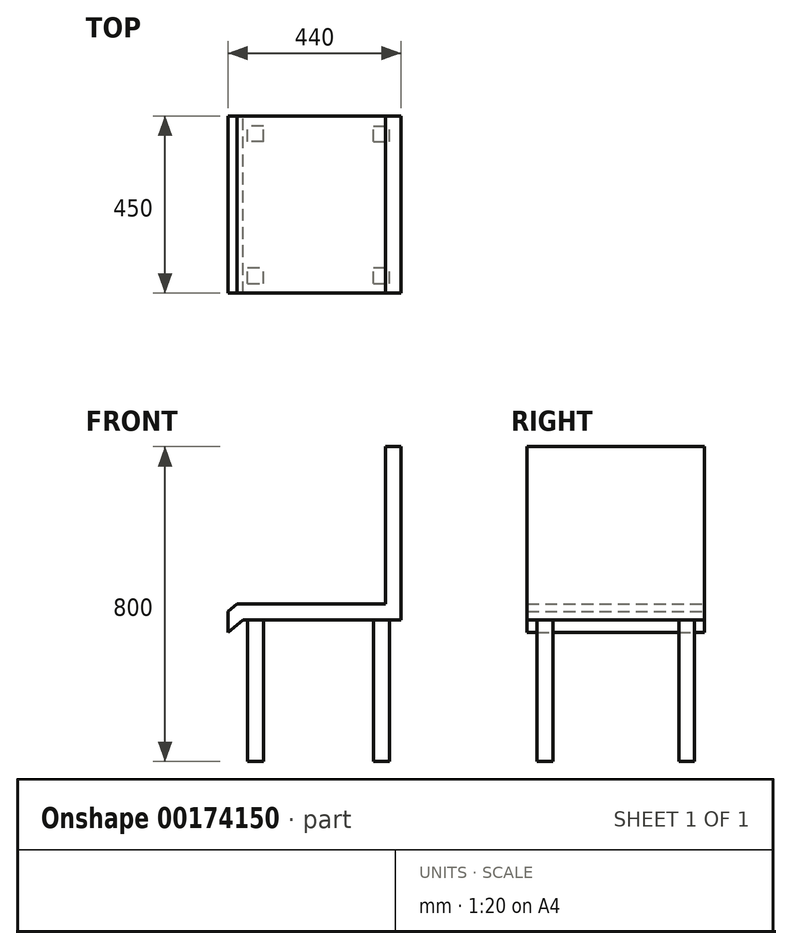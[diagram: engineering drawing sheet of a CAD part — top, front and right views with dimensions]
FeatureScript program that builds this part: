
annotation { "Feature Type Name" : "Feature", "Feature Type Description" : "" }
export const myFeature = defineFeature(function(context is Context, id is Id, definition is map)
    precondition{}
    {
        {
            var Q0;
            Q0=qCreatedBy(makeId("Front.planeOp"),FACE);
            var sketch = newSketch(context, id + "F0", { "sketchPlane" : qUnion([Q0])});
            skLineSegment(sketch, "E0", {"start": v(-250, 328.5) * mm, "end": v(-212.46, 360) * mm});
            skLineSegment(sketch, "E1", {"start": v(-212.46, 360) * mm, "end": v(190, 360) * mm});
            skLineSegment(sketch, "E2", {"start": v(190, 360) * mm, "end": v(190, 800) * mm});
            skLineSegment(sketch, "E3", {"start": v(190, 800) * mm, "end": v(150, 800) * mm});
            skLineSegment(sketch, "E4", {"start": v(150, 800) * mm, "end": v(150, 400) * mm});
            skLineSegment(sketch, "E5", {"start": v(150, 400) * mm, "end": v(-227.02, 400) * mm});
            skLineSegment(sketch, "E6", {"start": v(-227.02, 400) * mm, "end": v(-250, 380.72) * mm});
            skLineSegment(sketch, "E7", {"start": v(-250, 380.72) * mm, "end": v(-250, 328.5) * mm});
            skSolve(sketch);
        }
        {
            var Q0;
            Q0=makeQuery(id+"F0.imprint","IMPRINT",FACE,{"disambiguationData":[TD([[makeQuery(id+"F0.imprint","IMPRINT",EDGE,{"derivedFrom":sQuery(id+"F0.wireOp",EDGE,"E0")}),1.0]])]});
            extrude(context, id + "F1", {"entities" : qUnion([Q0]), "endBound" : BoundingType.SYMMETRIC, "depth" : 450 * mm});
        }
        {
            var Q0;
            Q0=qCreatedBy(makeId("Top.planeOp"),FACE);
            var sketch = newSketch(context, id + "F2", { "sketchPlane" : qUnion([Q0])});
            skLineSegment(sketch, "E8.bottom", {"start": v(-200, -200) * mm, "end": v(-160, -200) * mm});
            skLineSegment(sketch, "E8.top", {"start": v(-200, -160) * mm, "end": v(-160, -160) * mm});
            skLineSegment(sketch, "E8.left", {"start": v(-200, -200) * mm, "end": v(-200, -160) * mm});
            skLineSegment(sketch, "E8.right", {"start": v(-160, -200) * mm, "end": v(-160, -160) * mm});
            skLineSegment(sketch, "E9.bottom", {"start": v(120, -200) * mm, "end": v(160, -200) * mm});
            skLineSegment(sketch, "E9.top", {"start": v(120, -160) * mm, "end": v(160, -160) * mm});
            skLineSegment(sketch, "E9.left", {"start": v(120, -200) * mm, "end": v(120, -160) * mm});
            skLineSegment(sketch, "E9.right", {"start": v(160, -200) * mm, "end": v(160, -160) * mm});
            skLineSegment(sketch, "E10.bottom", {"start": v(-160, 160) * mm, "end": v(-200, 160) * mm});
            skLineSegment(sketch, "E10.top", {"start": v(-160, 200) * mm, "end": v(-200, 200) * mm});
            skLineSegment(sketch, "E10.left", {"start": v(-160, 160) * mm, "end": v(-160, 200) * mm});
            skLineSegment(sketch, "E10.right", {"start": v(-200, 160) * mm, "end": v(-200, 200) * mm});
            skLineSegment(sketch, "E11.bottom", {"start": v(120, 160) * mm, "end": v(160, 160) * mm});
            skLineSegment(sketch, "E11.top", {"start": v(120, 200) * mm, "end": v(160, 200) * mm});
            skLineSegment(sketch, "E11.left", {"start": v(120, 160) * mm, "end": v(120, 200) * mm});
            skLineSegment(sketch, "E11.right", {"start": v(160, 160) * mm, "end": v(160, 200) * mm});
            skSolve(sketch);
        }
        {
            var Q0;
            Q0=makeQuery(id+"F2.imprint","IMPRINT",FACE,{"disambiguationData":[TD([[makeQuery(id+"F2.imprint","IMPRINT",EDGE,{"derivedFrom":sQuery(id+"F2.wireOp",EDGE,"E9.bottom")}),1.0]])]});
            var Q1;
            Q1=makeQuery(id+"F2.imprint","IMPRINT",FACE,{"disambiguationData":[TD([[makeQuery(id+"F2.imprint","IMPRINT",EDGE,{"derivedFrom":sQuery(id+"F2.wireOp",EDGE,"E8.bottom")}),1.0]])]});
            var Q2;
            Q2=makeQuery(id+"F2.imprint","IMPRINT",FACE,{"disambiguationData":[TD([[makeQuery(id+"F2.imprint","IMPRINT",EDGE,{"derivedFrom":sQuery(id+"F2.wireOp",EDGE,"E10.bottom")}),-1.0]])]});
            var Q3;
            Q3=makeQuery(id+"F2.imprint","IMPRINT",FACE,{"disambiguationData":[TD([[makeQuery(id+"F2.imprint","IMPRINT",EDGE,{"derivedFrom":sQuery(id+"F2.wireOp",EDGE,"E11.bottom")}),1.0]])]});
            var Q4;
            Q4=makeQuery(id+"F1.opExtrude","SWEPT_BODY",BODY,{"disambiguationData":[OSD([sQuery(id+"F0.wireOp",EDGE,"E0"),sQuery(id+"F0.wireOp",EDGE,"E1"),sQuery(id+"F0.wireOp",EDGE,"E2"),sQuery(id+"F0.wireOp",EDGE,"E3"),sQuery(id+"F0.wireOp",EDGE,"E4"),sQuery(id+"F0.wireOp",EDGE,"E5"),sQuery(id+"F0.wireOp",EDGE,"E6"),sQuery(id+"F0.wireOp",EDGE,"E7")])]});
            extrude(context, id + "F3", {"entities" : qUnion([Q0, Q1, Q2, Q3]), "operationType" : NewBodyOperationType.ADD, "endBound" : BoundingType.UP_TO_BODY, "endBoundEntityBody" : qUnion([Q4]), "depth" : 25 * mm});
        }
    });
